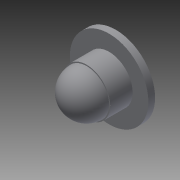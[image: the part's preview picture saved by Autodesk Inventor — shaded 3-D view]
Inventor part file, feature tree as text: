
AUTODESK INVENTOR PART (.ipt)
format: ipt  version: 2014 (Build 180170000, 170)  size: 109,056 bytes
history: native  units: mm
features: sketch x4, revolve x2, extrude x2, plane x1
ambient origin geometry x8: Origin, YZ Plane, XZ Plane, XY Plane, X Axis, Y Axis, Z Axis, Center Point
bodies: Solid1 (feature_tree)
feature tree (9):
  revolve  "Revolution1"  Angle=90.0deg
  plane  "Work Plane1"
  sketch  "Sketch2"  dims[d2=21.0mm d3=21.0mm]
  revolve  "Revolution2"  [1 undecoded]
  extrude  "Extrusion1"  Depth=10.0mm TaperAngle=0.0deg
  extrude  "Extrusion2"  Depth=3.0mm TaperAngle=0.0deg
  sketch  "Sketch1"  dims[d0=20.0mm d1=90.0deg]
  sketch  "Sketch3"  dims[d4=180.0deg d5=10.0mm d6=0.0mm]
  sketch  "Sketch4"  dims[d7=35.0mm d8=3.0mm d9=0.0mm]
note: 1 required parameter value undecoded (feature->parameter linkage not recoverable at this tier; creation-order binding heuristic only, values carry confidence <= 0.55)
